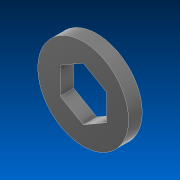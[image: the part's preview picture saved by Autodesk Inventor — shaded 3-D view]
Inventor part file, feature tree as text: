
AUTODESK INVENTOR PART (.ipt)
format: ipt  version: 2022.2 (Build 262287000, 287)  size: 95,232 bytes
history: native  units: in
note: dims shown in document units (in); Inventor stores cm internally (conversion verified against a paired STEP export)
features: extrude x1, sketch x1
ambient origin geometry x8: Origin, YZ Plane, XZ Plane, XY Plane, X Axis, Y Axis, Z Axis, Center Point
bodies: Solid1 (feature_tree)
feature tree (2):
  extrude  "Extrusion1"  Depth=0.15in
  sketch  "Sketch1"  dims[d0=0.51in d1=1.0in d2=0.15in d3=0.0in]
